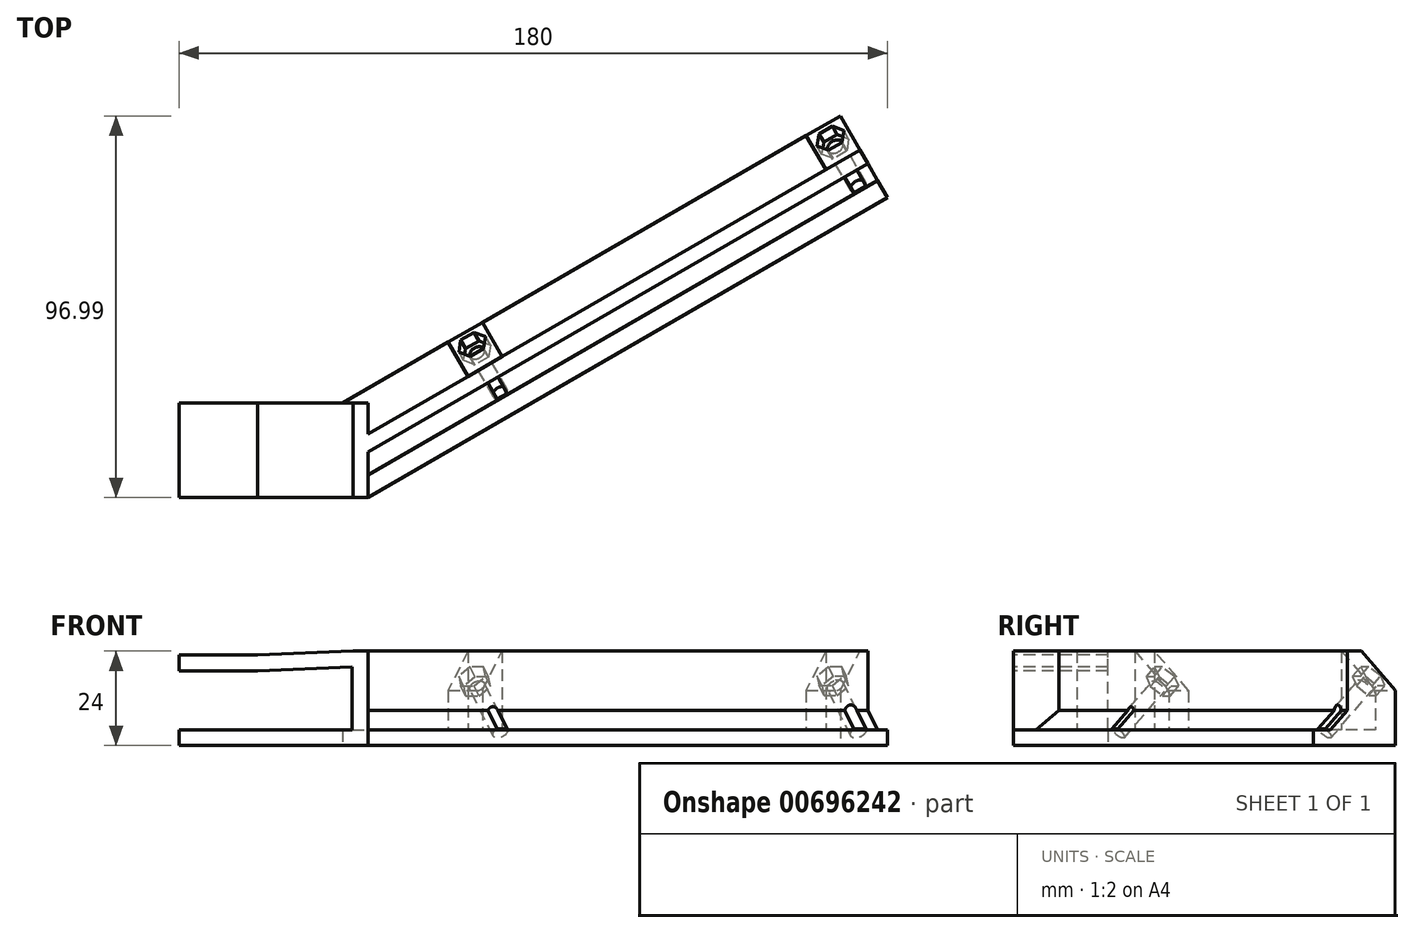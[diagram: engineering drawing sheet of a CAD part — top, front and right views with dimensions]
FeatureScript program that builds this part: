
annotation { "Feature Type Name" : "Feature", "Feature Type Description" : "" }
export const myFeature = defineFeature(function(context is Context, id is Id, definition is map)
    precondition{}
    {
        {
            var Q0;
            Q0=qCreatedBy(makeId("Top.planeOp"),FACE);
            var sketch = newSketch(context, id + "F0", { "sketchPlane" : qUnion([Q0])});
            skLineSegment(sketch, "E0.bottom", {"start": v(-77.3, 8.76) * mm, "end": v(-29.3, 8.76) * mm});
            skLineSegment(sketch, "E0.top", {"start": v(-77.3, -15.24) * mm, "end": v(-29.3, -15.24) * mm});
            skLineSegment(sketch, "E0.left", {"start": v(-77.3, 8.76) * mm, "end": v(-77.3, -15.24) * mm});
            skLineSegment(sketch, "E0.right", {"start": v(-29.3, 8.76) * mm, "end": v(-29.3, -15.24) * mm});
            skLineSegment(sketch, "E1", {"start": v(-29.3, -15.24) * mm, "end": v(102.7, 60.97) * mm});
            skLineSegment(sketch, "E2", {"start": v(102.7, 60.97) * mm, "end": v(90.7, 81.75) * mm});
            skLineSegment(sketch, "E3", {"start": v(90.7, 81.75) * mm, "end": v(-35.73, 8.76) * mm});
            skLineSegment(sketch, "E4", {"start": v(-35.73, 8.76) * mm, "end": v(-23.73, -12.03) * mm});
            skSolve(sketch);
        }
        {
            var Q0;
            Q0 = qSketchRegion(id + "F0", true);
            extrude(context, id + "F1", {"entities" : qUnion([Q0]), "depth" : 4 * mm, "offsetDistance" : 25 * mm});
        }
        {
            var Q0;
            Q0=makeQuery(id+"F1.opExtrude","SWEPT_FACE",FACE,{"disambiguationData":[OSD([sQuery(id+"F0.wireOp",EDGE,"E0.top")])]});
            var sketch = newSketch(context, id + "F2", { "sketchPlane" : qUnion([Q0])});
            skLineSegment(sketch, "E5.bottom", {"start": v(-29.3, 4) * mm, "end": v(-33.3, 4) * mm});
            skLineSegment(sketch, "E5.top", {"start": v(-29.3, 20) * mm, "end": v(-33.3, 20) * mm});
            skLineSegment(sketch, "E5.left", {"start": v(-29.3, 4) * mm, "end": v(-29.3, 20) * mm});
            skLineSegment(sketch, "E5.right", {"start": v(-33.3, 4) * mm, "end": v(-33.3, 20) * mm});
            skLineSegment(sketch, "E6", {"start": v(-77.3, 4) * mm, "end": v(-77.3, 19) * mm, "construction": true});
            skLineSegment(sketch, "E7", {"start": v(-57.3, 4) * mm, "end": v(-57.3, 19) * mm, "construction": true});
            skLineSegment(sketch, "E8.bottom", {"start": v(-77.3, 19) * mm, "end": v(-57.3, 19) * mm});
            skLineSegment(sketch, "E8.top", {"start": v(-77.3, 23) * mm, "end": v(-57.3, 23) * mm});
            skLineSegment(sketch, "E8.left", {"start": v(-77.3, 19) * mm, "end": v(-77.3, 23) * mm});
            skLineSegment(sketch, "E8.right", {"start": v(-57.3, 19) * mm, "end": v(-57.3, 23) * mm});
            skLineSegment(sketch, "E9", {"start": v(-29.3, 24) * mm, "end": v(-29.3, 20) * mm});
            skLineSegment(sketch, "E10", {"start": v(-29.3, 24) * mm, "end": v(-33.13, 24) * mm});
            skLineSegment(sketch, "E11", {"start": v(-57.3, 23) * mm, "end": v(-33.13, 24) * mm});
            skPoint(sketch, "E12.orphan", {"position": v(-36.96, 24) * mm});
            skLineSegment(sketch, "E13", {"start": v(-57.3, 19) * mm, "end": v(-33.3, 20) * mm});
            skSolve(sketch);
        }
        {
            var Q0;
            Q0 = qSketchRegion(id + "F2", true);
            extrude(context, id + "F3", {"entities" : qUnion([Q0]), "operationType" : NewBodyOperationType.ADD, "oppositeDirection" : true, "depth" : 24 * mm, "offsetDistance" : 25 * mm});
        }
        {
            var Q0;
            Q0=makeQuery(id+"F1.opExtrude","CAP_FACE",FACE,{"disambiguationData":[OSD([sQuery(id+"F0.wireOp",EDGE,"E0.bottom"),sQuery(id+"F0.wireOp",EDGE,"E0.top"),sQuery(id+"F0.wireOp",EDGE,"E0.left"),sQuery(id+"F0.wireOp",EDGE,"E1"),sQuery(id+"F0.wireOp",EDGE,"E2"),sQuery(id+"F0.wireOp",EDGE,"E3")])],"isStart":false});
            var sketch = newSketch(context, id + "F4", { "sketchPlane" : qUnion([Q0])});
            skLineSegment(sketch, "E14", {"start": v(97.7, 69.63) * mm, "end": v(95.7, 73.1) * mm});
            skLineSegment(sketch, "E15", {"start": v(95.7, 73.1) * mm, "end": v(-29.3, 0.92) * mm});
            skLineSegment(sketch, "E16", {"start": v(97.7, 69.63) * mm, "end": v(-29.3, -3.7) * mm});
            skLineSegment(sketch, "E17", {"start": v(-29.3, -3.7) * mm, "end": v(-29.3, 0.92) * mm});
            skSolve(sketch);
        }
        {
            var Q0;
            Q0 = qSketchRegion(id + "F4", true);
            extrude(context, id + "F5", {"entities" : qUnion([Q0]), "operationType" : NewBodyOperationType.ADD, "depth" : 20 * mm, "offsetDistance" : 25 * mm});
        }
        {
            var Q0;
            {var subQ10=sQuery(id+"F0.wireOp",EDGE,"E3");var subQ11=sQuery(id+"F0.wireOp",EDGE,"E0.bottom");var subQ12=sQuery(id+"F0.wireOp",EDGE,"E2");var subQ13=sQuery(id+"F0.wireOp",EDGE,"E0.top");var subQ14=sQuery(id+"F0.wireOp",EDGE,"E0.left");Q0=makeQuery(id+"F5.boolean.opBoolean","SPLIT",FACE,{"disambiguationData":[TD([makeQuery(id+"F1.opExtrude","SWEPT_FACE",FACE,{"disambiguationData":[OSD([subQ11])]})])],"derivedFrom":makeQuery(id+"F1.opExtrude","CAP_FACE",FACE,{"disambiguationData":[OSD([subQ11,subQ13,subQ14,sQuery(id+"F0.wireOp",EDGE,"E1"),subQ12,subQ10])],"isStart":false})});}
            var sketch = newSketch(context, id + "F6", { "sketchPlane" : qUnion([Q0])});
            skLineSegment(sketch, "E18", {"start": v(95.7, 73.1) * mm, "end": v(90.7, 81.75) * mm});
            skLineSegment(sketch, "E19", {"start": v(90.7, 81.75) * mm, "end": v(82.04, 76.75) * mm});
            skLineSegment(sketch, "E20", {"start": v(82.04, 76.75) * mm, "end": v(87.04, 68.1) * mm});
            skLineSegment(sketch, "E21", {"start": v(87.04, 68.1) * mm, "end": v(95.7, 73.1) * mm});
            skLineSegment(sketch, "E22", {"start": v(-0.24, 29.25) * mm, "end": v(4.76, 20.6) * mm});
            skLineSegment(sketch, "E23", {"start": v(4.76, 20.6) * mm, "end": v(-3.9, 15.6) * mm});
            skLineSegment(sketch, "E24", {"start": v(-3.9, 15.6) * mm, "end": v(-8.9, 24.25) * mm});
            skLineSegment(sketch, "E25", {"start": v(-8.9, 24.25) * mm, "end": v(-0.24, 29.25) * mm});
            skSolve(sketch);
        }
        {
            var Q0;
            Q0 = qSketchRegion(id + "F6", true);
            extrude(context, id + "F7", {"entities" : qUnion([Q0]), "operationType" : NewBodyOperationType.ADD, "depth" : 20 * mm, "offsetDistance" : 25 * mm});
        }
        {
            var Q0;
            Q0=makeQuery(id+"F7.opExtrude","CAP_EDGE",EDGE,{"disambiguationData":[OSD([sQuery(id+"F6.wireOp",EDGE,"E19")])],"isStart":false});
            var Q1;
            Q1=makeQuery(id+"F7.opExtrude","CAP_EDGE",EDGE,{"disambiguationData":[OSD([sQuery(id+"F6.wireOp",EDGE,"E25")])],"isStart":false});
            chamfer(context, id + "F8", {"entities" : qUnion([Q0, Q1]), "width" : 10 * mm, "tangentPropagation" : true});
        }
        {
            var Q0;
            Q0=makeQuery(id+"F5.opExtrude","CAP_EDGE",EDGE,{"disambiguationData":[OSD([sQuery(id+"F4.wireOp",EDGE,"E16")])],"isStart":true});
            var Q1;
            {var subQ0=sQuery(id+"F4.wireOp",EDGE,"E15");Q1=makeQuery(id+"F7.boolean.opBoolean","SPLIT",EDGE,{"disambiguationData":[TD([makeQuery(id+"F7.opExtrude","SWEPT_FACE",FACE,{"disambiguationData":[OSD([sQuery(id+"F6.wireOp",EDGE,"E20")])]})])],"derivedFrom":makeQuery(id+"F5.opExtrude","CAP_EDGE",EDGE,{"disambiguationData":[OSD([subQ0])],"isStart":true})});}
            chamfer(context, id + "F9", {"entities" : qUnion([Q0, Q1]), "width" : 5 * mm, "tangentPropagation" : true});
        }
        {
            var Q0;
            Q0=makeQuery(id+"F8.opChamfer","BLEND_FACE",FACE,{"disambiguationData":[OSD([sQuery(id+"F6.wireOp",EDGE,"E25")])]});
            var sketch = newSketch(context, id + "F10", { "sketchPlane" : qUnion([Q0])});
            skCircle(sketch, "E26", {"center": v(7.55, 6.43) * mm, "radius": 2 * mm});
            skCircle(sketch, "E27", {"center": v(104.82, 45.97) * mm, "radius": 2.16 * mm});
            skSolve(sketch);
        }
        {
            var Q0;
            Q0 = qSketchRegion(id + "F10", true);
            extrude(context, id + "F11", {"entities" : qUnion([Q0]), "operationType" : NewBodyOperationType.REMOVE, "oppositeDirection" : true, "depth" : 20.1 * mm, "offsetDistance" : 25 * mm});
        }
        {
            var Q0;
            Q0=makeQuery(id+"F8.opChamfer","BLEND_FACE",FACE,{"disambiguationData":[OSD([sQuery(id+"F6.wireOp",EDGE,"E19")])]});
            var sketch = newSketch(context, id + "F12", { "sketchPlane" : qUnion([Q0])});
            skCircle(sketch, "E28.cCircle", {"center": v(104.82, 45.97) * mm, "radius": 3.4 * mm, "construction": true});
            skLineSegment(sketch, "E28.0", {"start": v(104.3, 42.08) * mm, "end": v(101.19, 44.48) * mm});
            skLineSegment(sketch, "E28.1", {"start": v(101.19, 44.48) * mm, "end": v(101.72, 48.37) * mm});
            skLineSegment(sketch, "E28.2", {"start": v(101.72, 48.37) * mm, "end": v(105.35, 49.86) * mm});
            skLineSegment(sketch, "E28.3", {"start": v(105.35, 49.86) * mm, "end": v(108.46, 47.45) * mm});
            skLineSegment(sketch, "E28.4", {"start": v(108.46, 47.45) * mm, "end": v(107.92, 43.56) * mm});
            skLineSegment(sketch, "E28.5", {"start": v(107.92, 43.56) * mm, "end": v(104.3, 42.08) * mm});
            skPoint(sketch, "E28.0.midPoint", {"position": v(102.74, 43.28) * mm});
            skSolve(sketch);
        }
        {
            var Q0;
            Q0 = qSketchRegion(id + "F12", true);
            extrude(context, id + "F13", {"entities" : qUnion([Q0]), "operationType" : NewBodyOperationType.REMOVE, "oppositeDirection" : true, "depth" : 3.5 * mm, "offsetDistance" : 25 * mm});
        }
        {
            var Q0;
            Q0=makeQuery(id+"F8.opChamfer","BLEND_FACE",FACE,{"disambiguationData":[OSD([sQuery(id+"F6.wireOp",EDGE,"E25")])]});
            var sketch = newSketch(context, id + "F14", { "sketchPlane" : qUnion([Q0])});
            skCircle(sketch, "E29.cCircle", {"center": v(7.55, 6.43) * mm, "radius": 3.4 * mm, "construction": true});
            skLineSegment(sketch, "E29.0", {"start": v(7.02, 2.54) * mm, "end": v(3.92, 4.94) * mm});
            skLineSegment(sketch, "E29.1", {"start": v(3.92, 4.94) * mm, "end": v(4.45, 8.83) * mm});
            skLineSegment(sketch, "E29.2", {"start": v(4.45, 8.83) * mm, "end": v(8.08, 10.32) * mm});
            skLineSegment(sketch, "E29.3", {"start": v(8.08, 10.32) * mm, "end": v(11.19, 7.91) * mm});
            skLineSegment(sketch, "E29.4", {"start": v(11.19, 7.91) * mm, "end": v(10.65, 4.02) * mm});
            skLineSegment(sketch, "E29.5", {"start": v(10.65, 4.02) * mm, "end": v(7.02, 2.54) * mm});
            skPoint(sketch, "E29.0.midPoint", {"position": v(5.47, 3.74) * mm});
            skSolve(sketch);
        }
        {
            var Q0;
            Q0 = qSketchRegion(id + "F14", true);
            extrude(context, id + "F15", {"entities" : qUnion([Q0]), "operationType" : NewBodyOperationType.REMOVE, "oppositeDirection" : true, "depth" : 3.5 * mm, "offsetDistance" : 25 * mm});
        }
    });
